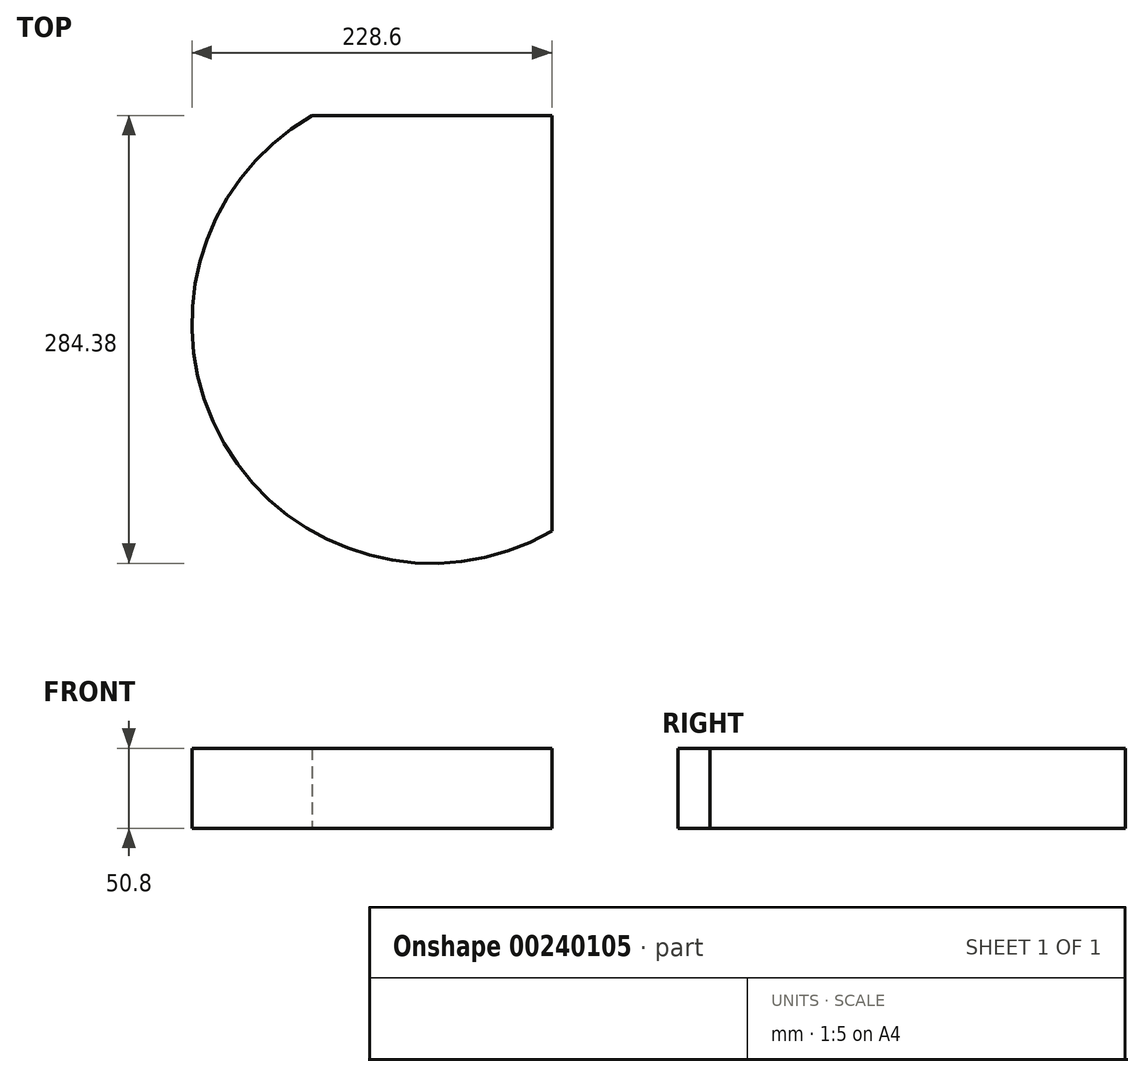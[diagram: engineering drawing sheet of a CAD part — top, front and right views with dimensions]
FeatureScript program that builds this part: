
annotation { "Feature Type Name" : "Feature", "Feature Type Description" : "" }
export const myFeature = defineFeature(function(context is Context, id is Id, definition is map)
    precondition{}
    {
        {
            var Q0;
            Q0=qCreatedBy(makeId("Top.planeOp"),FACE);
            var sketch = newSketch(context, id + "F0", { "sketchPlane" : qUnion([Q0])});
            skArc(sketch, "E0", {"start": v(-76.2, 131.98) * mm, "mid": v(-131.98, -76.2) * mm, "end": v(76.2, -131.98) * mm});
            skLineSegment(sketch, "E1", {"start": v(-76.2, 131.98) * mm, "end": v(76.2, 131.98) * mm});
            skLineSegment(sketch, "E2", {"start": v(76.2, 131.98) * mm, "end": v(76.2, -131.98) * mm});
            skSolve(sketch);
        }
        {
            var Q0;
            Q0 = qSketchRegion(id + "F0", true);
            extrude(context, id + "F1", {"entities" : qUnion([Q0]), "depth" : 50.8 * mm});
        }
    });
